# Revit family: Shower_Slide_Bar-GROHE-Tempesta-26077_Series
name_source: partatom
category: Plumbing Fixtures
units: mm (PartAtom-declared; Revit-internal decimal feet)

## family parameters
Cut with Voids When Loaded = No
Host = Face
OmniClass Number = 23.45.05.14.17
OmniClass Title = Showers
Part Type = Normal
Room Calculation Point = No
Round Connector Dimension = Use Diameter
Shared = Yes

## types (2) — shared parameters
(26 047) Tempesta Round 110 Hand Shower = Yes
(26 636) Union, recommended = Yes
(26 922) Tempesta 24” (600 mm) Shower Slide Bar = Yes
Adjustable Height = 18 1/2"
Adjustable Height Constraint = 18 1/2"
Adjustable Height Constraint /2 = 9 1/4"
Assembly Code = D2010710
CEC Compliant = Yes
CW Connection = No
CWFU = 3
CalGreen Compliant = Yes
Compliance Certifications = • WaterSense• CEC Certified• CALGreen Compliant• Massachusetts Plumbing Board Approved• Energy Policy Act of 1992• CSA B125.1• ASME A112.18.1
Default Elevation = 0"
Description = ROUND 110 24” SHOWER SLIDE BAR KIT - 2 SPRAYS
Flow Rate = 1.5gpm (5.7L/min)
HW Connection = No
HWFU = 3
Height = 18 1/2"
Holder Height from Base = 10"
Holder Height from Base Constraint = 8"
Installation Type = Wall Mounted
Manufacturer = Grohe
Tempered Connection Diameter = 1/2"
Type Comments = Adjustable hand shower holder glider
URL = https://www.grohe.com
Vent Connection = No
WFU = 4
Waste Connection = No
Width = 2 3/8"

## per-type parameters (varying)
| type | Finish | Material |
| 26077002 | Metal-Grohe-002-StarLight Chrome | Metal-Grohe-002-StarLight Chrome |
| 260772432 | Metal-Grohe-2431-Matte Black | Metal-Grohe-2431-Matte Black |

note: column(s) folded — value = type name in every type: Model

## geometry (parser evidence)
native form markers: Sweep x9
no freeform markers — native parametric forms only
